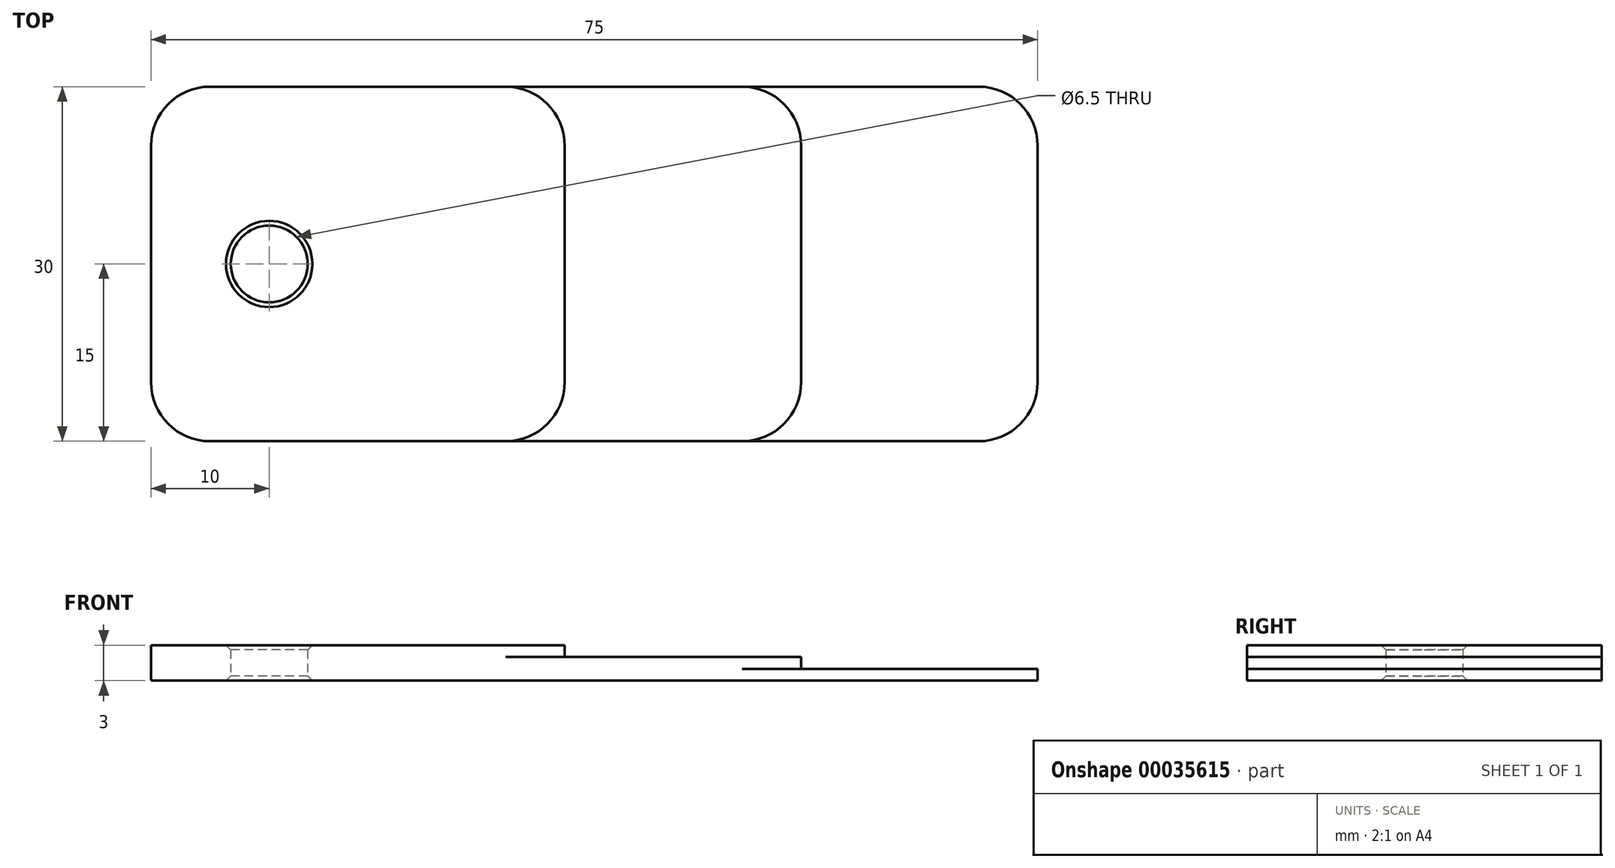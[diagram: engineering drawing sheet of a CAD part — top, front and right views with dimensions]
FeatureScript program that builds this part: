
annotation { "Feature Type Name" : "Feature", "Feature Type Description" : "" }
export const myFeature = defineFeature(function(context is Context, id is Id, definition is map)
    precondition{}
    {
        {
            var Q0;
            Q0=qCreatedBy(makeId("Top.planeOp"),FACE);
            var sketch = newSketch(context, id + "F0", { "sketchPlane" : qUnion([Q0])});
            skLineSegment(sketch, "E0.rect.bottom", {"start": v(-32.5, 15) * mm, "end": v(32.5, 15) * mm});
            skLineSegment(sketch, "E0.rect.top", {"start": v(-32.5, -15) * mm, "end": v(32.5, -15) * mm});
            skLineSegment(sketch, "E0.rect.left", {"start": v(-37.5, 10) * mm, "end": v(-37.5, -10) * mm});
            skLineSegment(sketch, "E0.rect.right", {"start": v(37.5, 10) * mm, "end": v(37.5, -10) * mm});
            skPoint(sketch, "E0.rect.middle", {"position": v(0, 0) * mm});
            skPoint(sketch, "E1.visualSharp", {"position": v(-37.5, 15) * mm});
            skArc(sketch, "E1.filletArc", {"start": v(-32.5, 15) * mm, "mid": v(-36.04, 13.54) * mm, "end": v(-37.5, 10) * mm});
            skPoint(sketch, "E2.visualSharp", {"position": v(-37.5, -15) * mm});
            skArc(sketch, "E2.filletArc", {"start": v(-37.5, -10) * mm, "mid": v(-36.04, -13.54) * mm, "end": v(-32.5, -15) * mm});
            skPoint(sketch, "E3.visualSharp", {"position": v(37.5, -15) * mm});
            skArc(sketch, "E3.filletArc", {"start": v(32.5, -15) * mm, "mid": v(36.04, -13.54) * mm, "end": v(37.5, -10) * mm});
            skPoint(sketch, "E4.visualSharp", {"position": v(37.5, 15) * mm});
            skArc(sketch, "E4.filletArc", {"start": v(37.5, 10) * mm, "mid": v(36.04, 13.54) * mm, "end": v(32.5, 15) * mm});
            skCircle(sketch, "E5", {"center": v(-27.5, 0) * mm, "radius": 3.25 * mm});
            skSolve(sketch);
        }
        {
            var Q0;
            Q0 = qSketchRegion(id + "F0", true);
            extrude(context, id + "F1", {"entities" : qUnion([Q0]), "depth" : 1 * mm});
        }
        {
            var Q0;
            Q0=makeQuery(id+"F1.opExtrude","CAP_FACE",FACE,{"disambiguationData":[OSD([sQuery(id+"F0.wireOp",EDGE,"E0.rect.bottom"),sQuery(id+"F0.wireOp",EDGE,"E0.rect.top"),sQuery(id+"F0.wireOp",EDGE,"E0.rect.left"),sQuery(id+"F0.wireOp",EDGE,"E0.rect.right"),sQuery(id+"F0.wireOp",EDGE,"E1.filletArc"),sQuery(id+"F0.wireOp",EDGE,"E2.filletArc"),sQuery(id+"F0.wireOp",EDGE,"E3.filletArc"),sQuery(id+"F0.wireOp",EDGE,"E4.filletArc"),sQuery(id+"F0.wireOp",EDGE,"E5")])],"isStart":false});
            var sketch = newSketch(context, id + "F2", { "sketchPlane" : qUnion([Q0])});
            skArc(sketch, "E6.0", {"start": v(-32.5, 15) * mm, "mid": v(-36.04, 13.54) * mm, "end": v(-37.5, 10) * mm});
            skLineSegment(sketch, "E7.0", {"start": v(-37.5, 10) * mm, "end": v(-37.5, -10) * mm});
            skArc(sketch, "E8.0", {"start": v(-37.5, -10) * mm, "mid": v(-36.04, -13.54) * mm, "end": v(-32.5, -15) * mm});
            skLineSegment(sketch, "E9.0", {"start": v(-32.5, -15) * mm, "end": v(12.5, -15) * mm});
            skLineSegment(sketch, "E10.0", {"start": v(-32.5, 15) * mm, "end": v(12.5, 15) * mm});
            skLineSegment(sketch, "E11", {"start": v(17.5, 10) * mm, "end": v(17.5, -10) * mm});
            skPoint(sketch, "E12.newPointA", {"position": v(32.5, 15) * mm});
            skArc(sketch, "E12.filletArc", {"start": v(17.5, 10) * mm, "mid": v(16.04, 13.54) * mm, "end": v(12.5, 15) * mm});
            skPoint(sketch, "E13.newPointA", {"position": v(32.5, -15) * mm});
            skArc(sketch, "E13.filletArc", {"start": v(12.5, -15) * mm, "mid": v(16.04, -13.54) * mm, "end": v(17.5, -10) * mm});
            skCircle(sketch, "E14.0", {"center": v(-27.5, 0) * mm, "radius": 3.25 * mm});
            skSolve(sketch);
        }
        {
            var Q0;
            Q0 = qSketchRegion(id + "F2", true);
            extrude(context, id + "F3", {"entities" : qUnion([Q0]), "operationType" : NewBodyOperationType.ADD, "depth" : 1 * mm});
        }
        {
            var Q0;
            Q0=makeQuery(id+"F3.opExtrude","CAP_FACE",FACE,{"disambiguationData":[OSD([sQuery(id+"F2.wireOp",EDGE,"E6.0"),sQuery(id+"F2.wireOp",EDGE,"E7.0"),sQuery(id+"F2.wireOp",EDGE,"E8.0"),sQuery(id+"F2.wireOp",EDGE,"E9.0"),sQuery(id+"F2.wireOp",EDGE,"E10.0"),sQuery(id+"F2.wireOp",EDGE,"E11"),sQuery(id+"F2.wireOp",EDGE,"E12.filletArc"),sQuery(id+"F2.wireOp",EDGE,"E13.filletArc"),sQuery(id+"F2.wireOp",EDGE,"E14.0")])],"isStart":false});
            var sketch = newSketch(context, id + "F4", { "sketchPlane" : qUnion([Q0])});
            skLineSegment(sketch, "E15.0", {"start": v(-32.5, 15) * mm, "end": v(-7.5, 15) * mm});
            skArc(sketch, "E16.0", {"start": v(-32.5, 15) * mm, "mid": v(-36.04, 13.54) * mm, "end": v(-37.5, 10) * mm});
            skLineSegment(sketch, "E17.0", {"start": v(-37.5, 10) * mm, "end": v(-37.5, -10) * mm});
            skArc(sketch, "E18.0", {"start": v(-37.5, -10) * mm, "mid": v(-36.04, -13.54) * mm, "end": v(-32.5, -15) * mm});
            skLineSegment(sketch, "E19.0", {"start": v(-32.5, -15) * mm, "end": v(-7.5, -15) * mm});
            skCircle(sketch, "E20.0", {"center": v(-27.5, 0) * mm, "radius": 3.25 * mm});
            skLineSegment(sketch, "E21", {"start": v(-2.5, 10) * mm, "end": v(-2.5, -10) * mm});
            skPoint(sketch, "E22.newPointA", {"position": v(32.5, 15) * mm});
            skArc(sketch, "E22.filletArc", {"start": v(-2.5, 10) * mm, "mid": v(-3.96, 13.54) * mm, "end": v(-7.5, 15) * mm});
            skPoint(sketch, "E23.newPointA", {"position": v(12.5, -15) * mm});
            skArc(sketch, "E23.filletArc", {"start": v(-7.5, -15) * mm, "mid": v(-3.96, -13.54) * mm, "end": v(-2.5, -10) * mm});
            skSolve(sketch);
        }
        {
            var Q0;
            Q0 = qSketchRegion(id + "F4", true);
            extrude(context, id + "F5", {"entities" : qUnion([Q0]), "operationType" : NewBodyOperationType.ADD, "depth" : 1 * mm});
        }
        {
            var Q0;
            Q0=makeQuery(id+"F5.opExtrude","CAP_EDGE",EDGE,{"disambiguationData":[OSD([sQuery(id+"F4.wireOp",EDGE,"E20.0")])],"isStart":false});
            var Q1;
            Q1=makeQuery(id+"F1.opExtrude","CAP_EDGE",EDGE,{"disambiguationData":[OSD([sQuery(id+"F0.wireOp",EDGE,"E5")])],"isStart":true});
            chamfer(context, id + "F6", {"entities" : qUnion([Q0, Q1]), "width" : .4 * mm, "tangentPropagation" : true});
        }
    });
